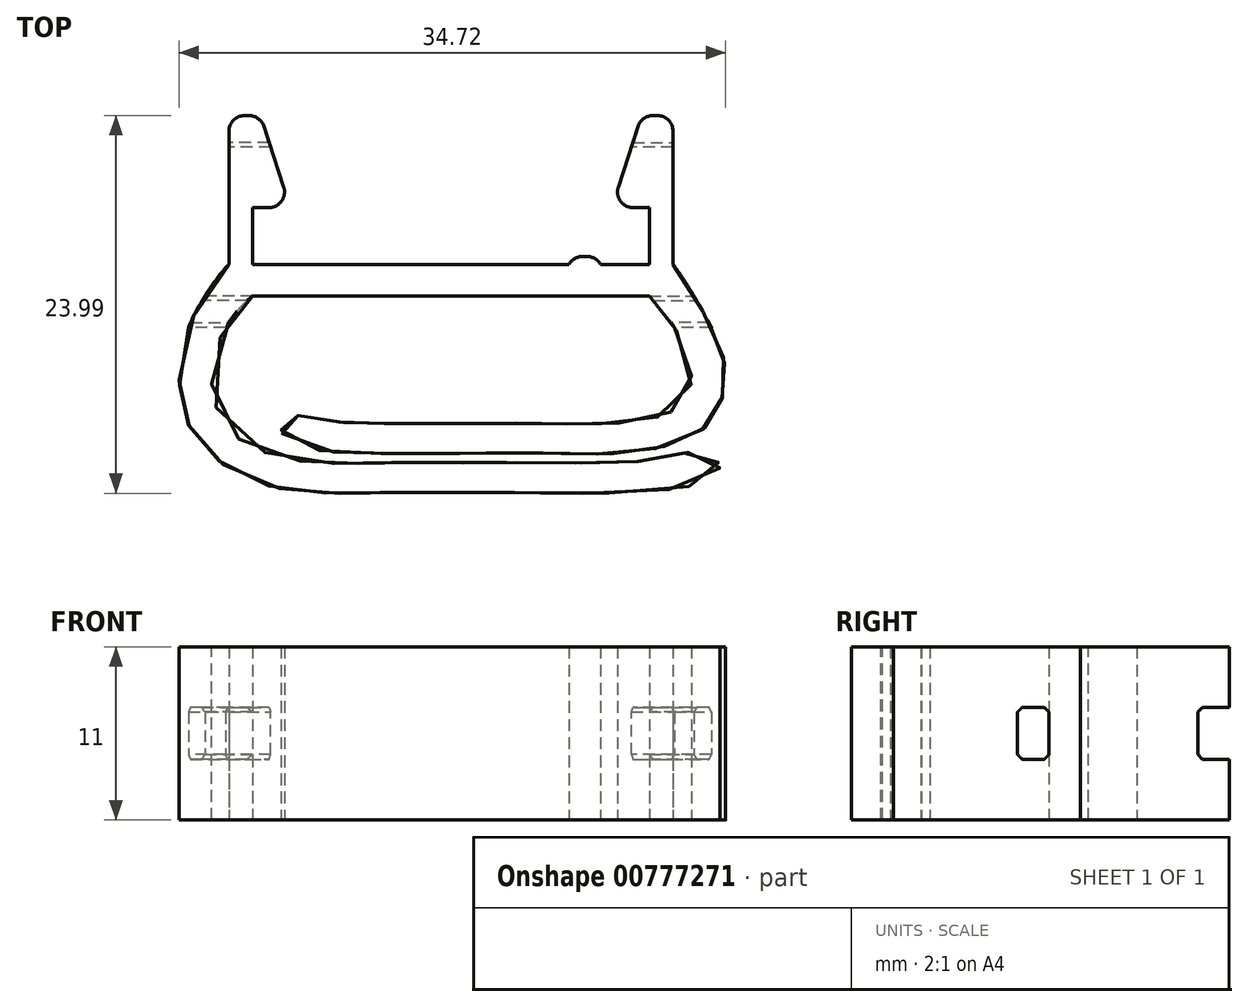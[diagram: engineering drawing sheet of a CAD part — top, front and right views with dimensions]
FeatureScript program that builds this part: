
annotation { "Feature Type Name" : "Feature", "Feature Type Description" : "" }
export const myFeature = defineFeature(function(context is Context, id is Id, definition is map)
    precondition{}
    {
        {
            var Q0;
            Q0=qCreatedBy(makeId("Top.planeOp"),FACE);
            var sketch = newSketch(context, id + "F0", { "sketchPlane" : qUnion([Q0])});
            skLineSegment(sketch, "E0", {"start": v(-14.1, 0) * mm, "end": v(-14.1, 9.45) * mm});
            skLineSegment(sketch, "E1", {"start": v(-14.1, 9.45) * mm, "end": v(-12.1, 9.45) * mm});
            skLineSegment(sketch, "E2", {"start": v(-12.1, 9.45) * mm, "end": v(-10.2, 3.6) * mm});
            skLineSegment(sketch, "E3", {"start": v(-10.2, 3.6) * mm, "end": v(-12.6, 3.6) * mm});
            skLineSegment(sketch, "E4", {"start": v(-12.6, 3.6) * mm, "end": v(-12.6, 0) * mm});
            skLineSegment(sketch, "E5", {"start": v(-12.6, 0) * mm, "end": v(0, 0) * mm});
            skLineSegment(sketch, "E6.MirrorCS", {"start": v(12.6, 0) * mm, "end": v(0, 0) * mm});
            skLineSegment(sketch, "E7.MirrorCS", {"start": v(12.6, 3.6) * mm, "end": v(12.6, 0) * mm});
            skLineSegment(sketch, "E8.MirrorCS", {"start": v(10.2, 3.6) * mm, "end": v(12.6, 3.6) * mm});
            skLineSegment(sketch, "E9.MirrorCS", {"start": v(12.1, 9.45) * mm, "end": v(10.2, 3.6) * mm});
            skLineSegment(sketch, "E10.MirrorCS", {"start": v(14.1, 9.45) * mm, "end": v(12.1, 9.45) * mm});
            skLineSegment(sketch, "E11.MirrorCS", {"start": v(14.1, 0) * mm, "end": v(14.1, 9.45) * mm});
            skLineSegment(sketch, "E12", {"start": v(-12.6, -2) * mm, "end": v(12.6, -2) * mm});
            skLineSegment(sketch, "E13.bottom", {"start": v(-9.5, 0) * mm, "end": v(-7.5, 0) * mm});
            skLineSegment(sketch, "E13.top", {"start": v(-9.5, 0.5) * mm, "end": v(-7.5, 0.5) * mm});
            skLineSegment(sketch, "E13.left", {"start": v(-9.5, 0) * mm, "end": v(-9.5, 0.5) * mm});
            skLineSegment(sketch, "E13.right", {"start": v(-7.5, 0) * mm, "end": v(-7.5, 0.5) * mm});
            skLineSegment(sketch, "E14.MirrorCS", {"start": v(9.5, 0) * mm, "end": v(9.5, 0.5) * mm});
            skLineSegment(sketch, "E15.MirrorCS", {"start": v(9.5, 0.5) * mm, "end": v(7.5, 0.5) * mm});
            skLineSegment(sketch, "E16.MirrorCS", {"start": v(7.5, 0) * mm, "end": v(7.5, 0.5) * mm});
            skFitSpline(sketch, "E17", {"points": [v(-14.1, 0) * mm, v(-16.87, -4.53) * mm, v(-17.1, -8.78) * mm, v(-16.28, -10.86) * mm, v(-13.22, -13.47) * mm, v(-8.6, -14.5) * mm, v(-4.16, -14.5) * mm, v(0, -14.5) * mm, v(4.08, -14.5) * mm, v(10.62, -14.5) * mm, v(17, -13.24) * mm, v(16.4, -12) * mm, v(13.76, -12.23) * mm, v(10.18, -12.6) * mm, v(4.25, -12.6) * mm, v(0, -12.6) * mm, v(-4.14, -12.6) * mm, v(-8.49, -12.6) * mm, v(-14.1, -10.53) * mm, v(-14.78, -4.9) * mm, v(-12.6, -2) * mm], "startDerivative": vector(-36.04, -32.7) * mm, "endDerivative": vector(28.45, 21.4) * mm});
            skPoint(sketch, "E18.5.internal.snap0", {"position": v(-11.15, 6.52) * mm});
            skPoint(sketch, "E18.6.internal.snap0", {"position": v(-11.15, 6.52) * mm});
            skFitSpline(sketch, "E18", {"points": [v(12.6, -2) * mm, v(14.46, -4.45) * mm, v(14.94, -8.56) * mm, v(10.88, -10.06) * mm, v(5.87, -10.1) * mm, v(1.52, -10.1) * mm, v(-2.3, -10.1) * mm, v(-5.05, -10.1) * mm, v(-8.9, -9.8) * mm, v(-10.45, -9.69) * mm, v(-10.57, -11.02) * mm, v(-4.78, -12) * mm, v(-2.32, -12) * mm, v(1.28, -12) * mm, v(6.14, -12) * mm, v(10.69, -12) * mm, v(15.38, -10.89) * mm, v(16.96, -9.2) * mm, v(17.44, -6.93) * mm, v(16.57, -4.05) * mm, v(14.1, 0) * mm], "startDerivative": vector(21.9, -31.42) * mm, "endDerivative": vector(-31.4, 40.84) * mm});
            skLineSegment(sketch, "E19", {"start": v(-15.17, -14) * mm, "end": v(17.67, -14) * mm, "construction": true});
            skLineSegment(sketch, "E20", {"start": v(-11.06, -12) * mm, "end": v(21.97, -12) * mm, "construction": true});
            skSolve(sketch);
        }
        {
            var Q0;
            Q0=makeQuery(id+"F0.imprint","IMPRINT",FACE,{"disambiguationData":[TD([[makeQuery(id+"F0.imprint","IMPRINT",EDGE,{"derivedFrom":sQuery(id+"F0.wireOp",EDGE,"E0")}),-1.0]])]});
            var Q1;
            Q1=makeQuery(id+"F0.imprint","IMPRINT",FACE,{"disambiguationData":[TD([[makeQuery(id+"F0.imprint","IMPRINT",EDGE,{"derivedFrom":sQuery(id+"F0.wireOp",EDGE,"E13.bottom")}),1.0]])]});
            var Q2;
            {var subQ0=sQuery(id+"F0.wireOp",EDGE,"E14.MirrorCS");Q2=makeQuery(id+"F0.imprint","IMPRINT",FACE,{"disambiguationData":[TD([[makeQuery(id+"F0.imprint","IMPRINT",EDGE,{"derivedFrom":subQ0}),1.0]])]});}
            extrude(context, id + "F1", {"entities" : qUnion([Q0, Q1, Q2]), "depth" : 11 * mm, "offsetDistance" : 25 * mm});
        }
        {
            var Q0;
            Q0=makeQuery(id+"F1.opExtrude","SWEPT_EDGE",EDGE,{"disambiguationData":[OSD([sQuery(id+"F0.wireOp",EDGE,"E2"),sQuery(id+"F0.wireOp",EDGE,"E3")])]});
            var Q1;
            Q1=makeQuery(id+"F1.opExtrude","SWEPT_EDGE",EDGE,{"disambiguationData":[OSD([sQuery(id+"F0.wireOp",EDGE,"E0"),sQuery(id+"F0.wireOp",EDGE,"E1")])]});
            var Q2;
            Q2=makeQuery(id+"F1.opExtrude","SWEPT_EDGE",EDGE,{"disambiguationData":[OSD([sQuery(id+"F0.wireOp",EDGE,"E1"),sQuery(id+"F0.wireOp",EDGE,"E2")])]});
            var Q3;
            Q3=makeQuery(id+"F1.opExtrude","SWEPT_EDGE",EDGE,{"disambiguationData":[OSD([sQuery(id+"F0.wireOp",EDGE,"E13.top"),sQuery(id+"F0.wireOp",EDGE,"E13.left")])]});
            var Q4;
            Q4=makeQuery(id+"F1.opExtrude","SWEPT_EDGE",EDGE,{"disambiguationData":[OSD([sQuery(id+"F0.wireOp",EDGE,"E13.top"),sQuery(id+"F0.wireOp",EDGE,"E13.right")])]});
            var Q5;
            Q5=makeQuery(id+"F1.opExtrude","SWEPT_EDGE",EDGE,{"disambiguationData":[OSD([sQuery(id+"F0.wireOp",EDGE,"E15.MirrorCS"),sQuery(id+"F0.wireOp",EDGE,"E16.MirrorCS")])]});
            var Q6;
            Q6=makeQuery(id+"F1.opExtrude","SWEPT_EDGE",EDGE,{"disambiguationData":[OSD([sQuery(id+"F0.wireOp",EDGE,"E14.MirrorCS"),sQuery(id+"F0.wireOp",EDGE,"E15.MirrorCS")])]});
            var Q7;
            Q7=makeQuery(id+"F1.opExtrude","SWEPT_EDGE",EDGE,{"disambiguationData":[OSD([sQuery(id+"F0.wireOp",EDGE,"E8.MirrorCS"),sQuery(id+"F0.wireOp",EDGE,"E9.MirrorCS")])]});
            var Q8;
            Q8=makeQuery(id+"F1.opExtrude","SWEPT_EDGE",EDGE,{"disambiguationData":[OSD([sQuery(id+"F0.wireOp",EDGE,"E9.MirrorCS"),sQuery(id+"F0.wireOp",EDGE,"E10.MirrorCS")])]});
            var Q9;
            Q9=makeQuery(id+"F1.opExtrude","SWEPT_EDGE",EDGE,{"disambiguationData":[OSD([sQuery(id+"F0.wireOp",EDGE,"E10.MirrorCS"),sQuery(id+"F0.wireOp",EDGE,"E11.MirrorCS")])]});
            fillet(context, id + "F2", {"entities" : qUnion([Q0, Q1, Q2, Q3, Q4, Q5, Q6, Q7, Q8, Q9]), "radius" : 1 * mm, "tangentPropagation" : true, "allowEdgeOverflow" : false});
        }
        {
            var Q0;
            Q0=qCreatedBy(makeId("Right.planeOp"),FACE);
            var sketch = newSketch(context, id + "F3", { "sketchPlane" : qUnion([Q0])});
            skLineSegment(sketch, "E21.bottom", {"start": v(-4, 3.85) * mm, "end": v(-2, 3.85) * mm});
            skLineSegment(sketch, "E21.top", {"start": v(-4, 7.15) * mm, "end": v(-2, 7.15) * mm});
            skLineSegment(sketch, "E21.left", {"start": v(-4, 3.85) * mm, "end": v(-4, 7.15) * mm});
            skLineSegment(sketch, "E21.right", {"start": v(-2, 3.85) * mm, "end": v(-2, 7.15) * mm});
            skPoint(sketch, "E21.middle", {"position": v(-3, 5.5) * mm});
            skLineSegment(sketch, "E22.bottom", {"start": v(7.45, 3.85) * mm, "end": v(9.45, 3.85) * mm});
            skLineSegment(sketch, "E22.top", {"start": v(7.45, 7.15) * mm, "end": v(9.45, 7.15) * mm});
            skLineSegment(sketch, "E22.left", {"start": v(7.45, 3.85) * mm, "end": v(7.45, 7.15) * mm});
            skLineSegment(sketch, "E22.right", {"start": v(9.45, 3.85) * mm, "end": v(9.45, 7.15) * mm});
            skPoint(sketch, "E22.middle", {"position": v(8.45, 5.5) * mm});
            skSolve(sketch);
        }
        {
            var Q0;
            Q0=qSketchRegion(id+"F3",true);
            extrude(context, id + "F4", {"entities" : qUnion([Q0]), "operationType" : NewBodyOperationType.REMOVE, "endBound" : BoundingType.SYMMETRIC, "oppositeDirection" : true, "depth" : 35 * mm, "offsetDistance" : 25 * mm});
        }
        {
            var Q0;
            {var subQ0=sQuery(id+"F3.wireOp",EDGE,"E21.bottom");var subQ1=sQuery(id+"F3.wireOp",EDGE,"E21.left");Q0=makeQuery(id+"F4.boolean.opBoolean","COPY",EDGE,{"disambiguationData":[TD([makeQuery(id+"F1.opExtrude","SWEPT_FACE",FACE,{"disambiguationData":[OSD([sQuery(id+"F0.wireOp",EDGE,"E17")])]})])],"derivedFrom":makeQuery(id+"F4.opExtrude","SWEPT_EDGE",EDGE,{"disambiguationData":[OSD([subQ0,subQ1])]})});}
            var Q1;
            {var subQ0=sQuery(id+"F3.wireOp",EDGE,"E21.top");var subQ1=sQuery(id+"F3.wireOp",EDGE,"E21.right");Q1=makeQuery(id+"F4.boolean.opBoolean","COPY",EDGE,{"disambiguationData":[TD([makeQuery(id+"F1.opExtrude","SWEPT_FACE",FACE,{"disambiguationData":[OSD([sQuery(id+"F0.wireOp",EDGE,"E17")])]})])],"derivedFrom":makeQuery(id+"F4.opExtrude","SWEPT_EDGE",EDGE,{"disambiguationData":[OSD([subQ0,subQ1])]})});}
            var Q2;
            {var subQ0=sQuery(id+"F3.wireOp",EDGE,"E21.top");var subQ1=sQuery(id+"F3.wireOp",EDGE,"E21.left");Q2=makeQuery(id+"F4.boolean.opBoolean","COPY",EDGE,{"disambiguationData":[TD([makeQuery(id+"F1.opExtrude","SWEPT_FACE",FACE,{"disambiguationData":[OSD([sQuery(id+"F0.wireOp",EDGE,"E17")])]})])],"derivedFrom":makeQuery(id+"F4.opExtrude","SWEPT_EDGE",EDGE,{"disambiguationData":[OSD([subQ0,subQ1])]})});}
            var Q3;
            {var subQ0=sQuery(id+"F3.wireOp",EDGE,"E21.bottom");var subQ1=sQuery(id+"F3.wireOp",EDGE,"E21.right");Q3=makeQuery(id+"F4.boolean.opBoolean","COPY",EDGE,{"disambiguationData":[TD([makeQuery(id+"F1.opExtrude","SWEPT_FACE",FACE,{"disambiguationData":[OSD([sQuery(id+"F0.wireOp",EDGE,"E17")])]})])],"derivedFrom":makeQuery(id+"F4.opExtrude","SWEPT_EDGE",EDGE,{"disambiguationData":[OSD([subQ0,subQ1])]})});}
            var Q4;
            {var subQ0=sQuery(id+"F3.wireOp",EDGE,"E22.bottom");var subQ1=sQuery(id+"F3.wireOp",EDGE,"E22.left");Q4=makeQuery(id+"F4.boolean.opBoolean","COPY",EDGE,{"disambiguationData":[TD([makeQuery(id+"F1.opExtrude","SWEPT_FACE",FACE,{"disambiguationData":[OSD([sQuery(id+"F0.wireOp",EDGE,"E0")])]})])],"derivedFrom":makeQuery(id+"F4.opExtrude","SWEPT_EDGE",EDGE,{"disambiguationData":[OSD([subQ0,subQ1])]})});}
            var Q5;
            {var subQ0=sQuery(id+"F3.wireOp",EDGE,"E22.top");var subQ1=sQuery(id+"F3.wireOp",EDGE,"E22.left");Q5=makeQuery(id+"F4.boolean.opBoolean","COPY",EDGE,{"disambiguationData":[TD([makeQuery(id+"F1.opExtrude","SWEPT_FACE",FACE,{"disambiguationData":[OSD([sQuery(id+"F0.wireOp",EDGE,"E0")])]})])],"derivedFrom":makeQuery(id+"F4.opExtrude","SWEPT_EDGE",EDGE,{"disambiguationData":[OSD([subQ0,subQ1])]})});}
            var Q6;
            {var subQ0=sQuery(id+"F3.wireOp",EDGE,"E22.left");var subQ1=sQuery(id+"F3.wireOp",EDGE,"E22.top");Q6=makeQuery(id+"F4.boolean.opBoolean","COPY",EDGE,{"disambiguationData":[TD([makeQuery(id+"F1.opExtrude","SWEPT_FACE",FACE,{"disambiguationData":[OSD([sQuery(id+"F0.wireOp",EDGE,"E9.MirrorCS")])]})])],"derivedFrom":makeQuery(id+"F4.opExtrude","SWEPT_EDGE",EDGE,{"disambiguationData":[OSD([subQ1,subQ0])]})});}
            var Q7;
            {var subQ0=sQuery(id+"F3.wireOp",EDGE,"E22.left");var subQ1=sQuery(id+"F3.wireOp",EDGE,"E22.bottom");Q7=makeQuery(id+"F4.boolean.opBoolean","COPY",EDGE,{"disambiguationData":[TD([makeQuery(id+"F1.opExtrude","SWEPT_FACE",FACE,{"disambiguationData":[OSD([sQuery(id+"F0.wireOp",EDGE,"E9.MirrorCS")])]})])],"derivedFrom":makeQuery(id+"F4.opExtrude","SWEPT_EDGE",EDGE,{"disambiguationData":[OSD([subQ1,subQ0])]})});}
            var Q8;
            {var subQ0=sQuery(id+"F3.wireOp",EDGE,"E21.top");var subQ1=sQuery(id+"F3.wireOp",EDGE,"E21.right");Q8=makeQuery(id+"F4.boolean.opBoolean","COPY",EDGE,{"disambiguationData":[TD([makeQuery(id+"F1.opExtrude","SWEPT_FACE",FACE,{"disambiguationData":[OSD([sQuery(id+"F0.wireOp",EDGE,"E18")])]})])],"derivedFrom":makeQuery(id+"F4.opExtrude","SWEPT_EDGE",EDGE,{"disambiguationData":[OSD([subQ0,subQ1])]})});}
            var Q9;
            {var subQ0=sQuery(id+"F3.wireOp",EDGE,"E21.top");var subQ1=sQuery(id+"F3.wireOp",EDGE,"E21.left");Q9=makeQuery(id+"F4.boolean.opBoolean","COPY",EDGE,{"disambiguationData":[TD([makeQuery(id+"F1.opExtrude","SWEPT_FACE",FACE,{"disambiguationData":[OSD([sQuery(id+"F0.wireOp",EDGE,"E18")])]})])],"derivedFrom":makeQuery(id+"F4.opExtrude","SWEPT_EDGE",EDGE,{"disambiguationData":[OSD([subQ0,subQ1])]})});}
            var Q10;
            {var subQ0=sQuery(id+"F3.wireOp",EDGE,"E21.bottom");var subQ1=sQuery(id+"F3.wireOp",EDGE,"E21.left");Q10=makeQuery(id+"F4.boolean.opBoolean","COPY",EDGE,{"disambiguationData":[TD([makeQuery(id+"F1.opExtrude","SWEPT_FACE",FACE,{"disambiguationData":[OSD([sQuery(id+"F0.wireOp",EDGE,"E18")])]})])],"derivedFrom":makeQuery(id+"F4.opExtrude","SWEPT_EDGE",EDGE,{"disambiguationData":[OSD([subQ0,subQ1])]})});}
            var Q11;
            {var subQ0=sQuery(id+"F3.wireOp",EDGE,"E21.bottom");var subQ1=sQuery(id+"F3.wireOp",EDGE,"E21.right");Q11=makeQuery(id+"F4.boolean.opBoolean","COPY",EDGE,{"disambiguationData":[TD([makeQuery(id+"F1.opExtrude","SWEPT_FACE",FACE,{"disambiguationData":[OSD([sQuery(id+"F0.wireOp",EDGE,"E18")])]})])],"derivedFrom":makeQuery(id+"F4.opExtrude","SWEPT_EDGE",EDGE,{"disambiguationData":[OSD([subQ0,subQ1])]})});}
            chamfer(context, id + "F5", {"entities" : qUnion([Q0, Q1, Q2, Q3, Q4, Q5, Q6, Q7, Q8, Q9, Q10, Q11]), "width" : .3 * mm, "tangentPropagation" : true});
        }
    });
